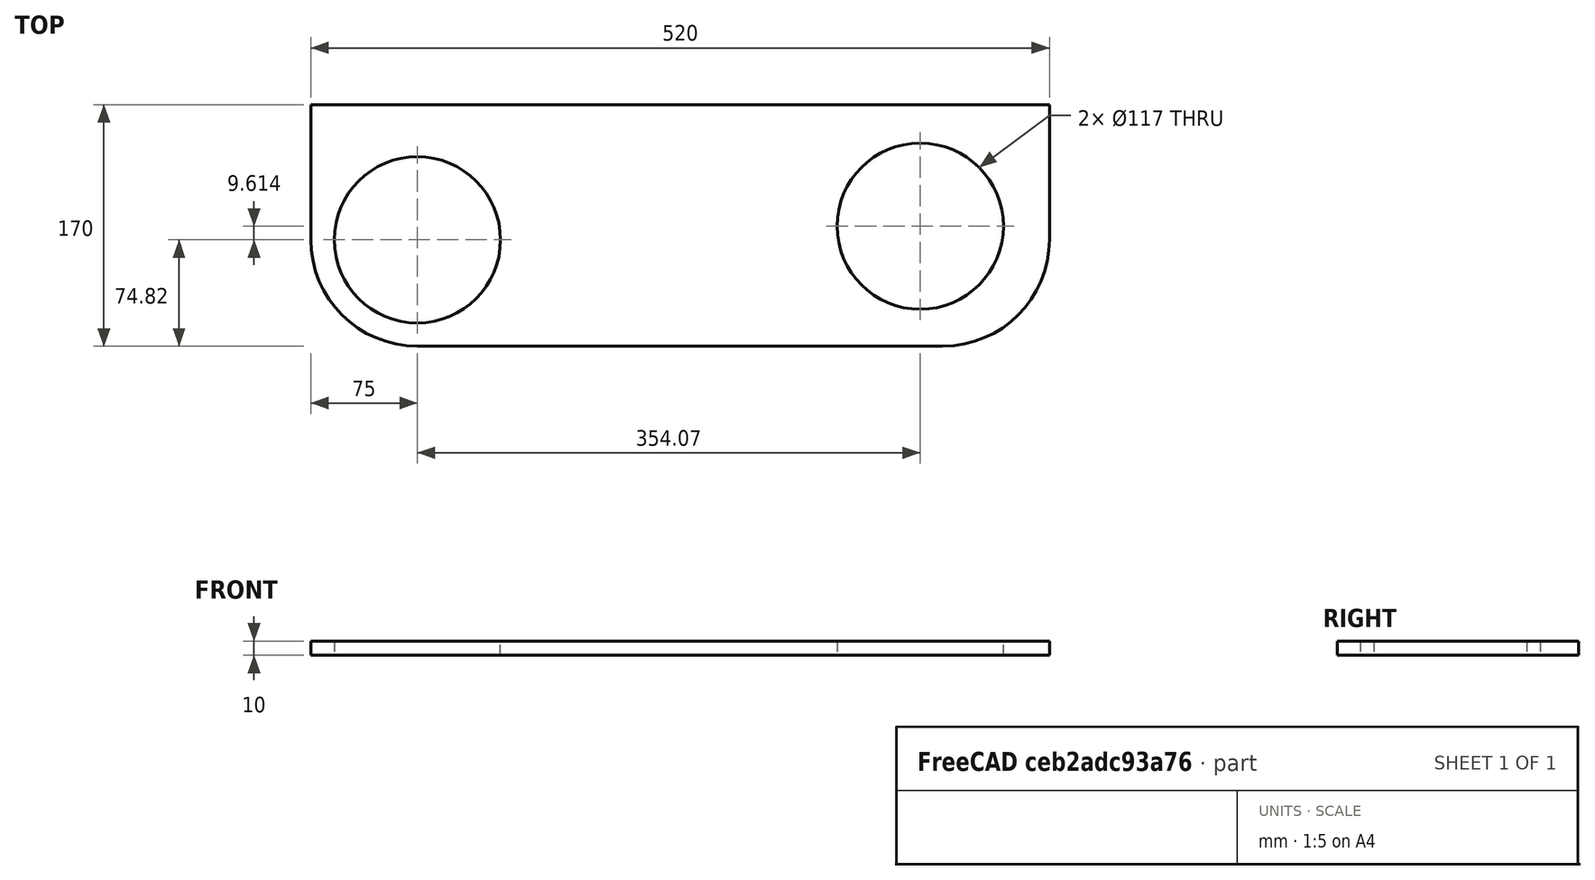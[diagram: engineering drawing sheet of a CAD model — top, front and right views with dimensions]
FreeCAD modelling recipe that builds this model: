
FCSTD DOCUMENT  (FreeCAD 1.0R39319 (Git))
Label: comp21_16mm_plate
License: All rights reserved
LicenseURL: https://en.wikipedia.org/wiki/All_rights_reserved
objects: Sketcher::SketchObject×1, PartDesign::Pad×1, PartDesign::Body×1
note: 6 computed .brp shape members not serialized (recipe doc carries the construction recipe); baked Part::Feature solids carry a one-line shape summary decoded from their .brp

FEATURE [Sketcher::SketchObject] Sketch
  ArcFitTolerance = 1e-06
  AttachmentSupport = -> [XY_Plane]
  FullyConstrained = true
  MakeInternals = false
  MapMode = 5
  sketch-geometry (10):
    g0: LineSegment StartX=75 StartY=0 StartZ=0 EndX=445 EndY=0 EndZ=0
    g1: LineSegment StartX=520 StartY=75 StartZ=0 EndX=520 EndY=170 EndZ=0
    g2: LineSegment StartX=520 StartY=170 StartZ=0 EndX=0 EndY=170 EndZ=0
    g3: LineSegment StartX=0 StartY=170 StartZ=0 EndX=0 EndY=75 EndZ=0
    g4: Circle CenterX=75 CenterY=74.82 CenterZ=0 NormalX=0 NormalY=0 NormalZ=1 AngleXU=0 Radius=58.5
    g5: Circle CenterX=429.07 CenterY=84.434 CenterZ=0 NormalX=0 NormalY=0 NormalZ=1 AngleXU=0 Radius=58.5
    g6: ArcOfCircle CenterX=75 CenterY=75 CenterZ=0 NormalX=0 NormalY=0 NormalZ=1 AngleXU=0 Radius=75 StartAngle=3.14159 EndAngle=4.71239
    g7: GeomPoint [constr] X=0 Y=0 Z=0
    g8: ArcOfCircle CenterX=445 CenterY=75 CenterZ=0 NormalX=0 NormalY=0 NormalZ=1 AngleXU=0 Radius=75 StartAngle=4.71239 EndAngle=6.28319
    g9: GeomPoint [constr] X=520 Y=0 Z=0
  constraints (25):
    c: Coincident(g1,g2)
    c: Coincident(g2,g3)
    c: Horizontal(g0)
    c: Horizontal(g2)
    c: Vertical(g1)
    c: Vertical(g3)
    c: Coincident(g7,g-1)
    c: DistanceX(g2,g2) = 520
    c: DistanceY(g7,g3) = 170
    c: Diameter(g4) = 117
    c: Equal(g4,g5)
    c: Distance(g5,g1) = 90.9305
    c: Distance(g5,g0) = 84.434
    c: DistanceY(g-1,g4) = 74.82
    c: Distance(g4,g3) = 75
    c: PointOnObject(g7,g3)
    c: PointOnObject(g7,g0)
    c: Tangent(g3,g6) = -1.5708
    c: Tangent(g0,g6) = -1.5708
    c: PointOnObject(g9,g1)
    c: PointOnObject(g9,g0)
    c: Tangent(g1,g8) = -1.5708
    c: Tangent(g0,g8) = -1.5708
    c: Radius(g6) = 75
    c: Radius(g8) = 75
FEATURE [PartDesign::Pad] Pad
  Direction = (0,0,1)
  Length = 10
  Length2 = 10
  Profile = -> Sketch
  ReferenceAxis = -> Sketch [N_Axis]
  Refine = true
  Suppressed = false
  Type = 0
FEATURE [PartDesign::Body] Body
  AllowCompound = false
  Group = -> [Sketch,Pad]
  Origin = -> Origin
  Tip = -> Pad
